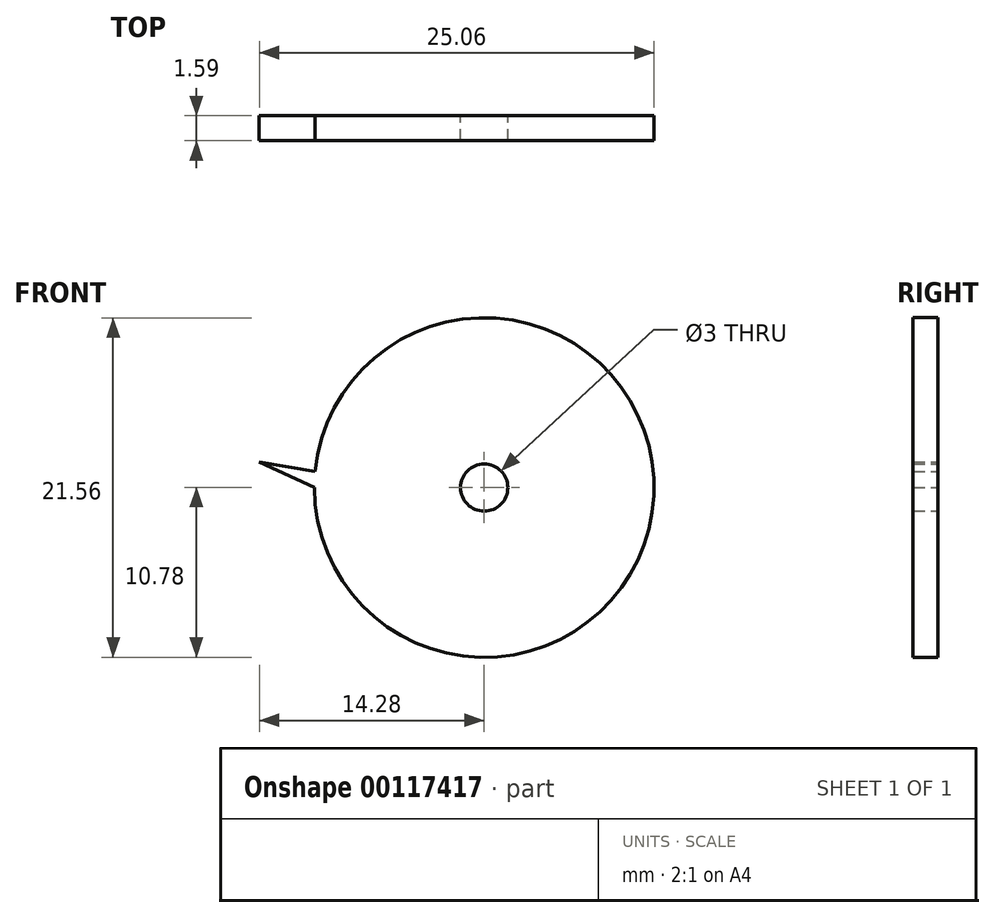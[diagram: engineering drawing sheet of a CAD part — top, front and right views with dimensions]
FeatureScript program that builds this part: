
annotation { "Feature Type Name" : "Feature", "Feature Type Description" : "" }
export const myFeature = defineFeature(function(context is Context, id is Id, definition is map)
    precondition{}
    {
        {
            var Q0;
            Q0=qCreatedBy(makeId("Front.planeOp"),FACE);
            var sketch = newSketch(context, id + "F0", { "sketchPlane" : qUnion([Q0])});
            skCircle(sketch, "E0", {"center": v(0, 0) * mm, "radius": 10.78 * mm});
            skLineSegment(sketch, "E1", {"start": v(-10.78, 0) * mm, "end": v(-14.28, 1.63) * mm});
            skPoint(sketch, "E2.endSnap0", {"position": v(-12.53, 0.82) * mm});
            skLineSegment(sketch, "E3", {"start": v(-14.28, 1.63) * mm, "end": v(-10.74, 1) * mm});
            skCircle(sketch, "E4", {"center": v(0, 0) * mm, "radius": 1.5 * mm});
            skLineSegment(sketch, "E5", {"start": v(-23.85, 0) * mm, "end": v(-3.39, 0) * mm});
            skSolve(sketch);
        }
        {
            var Q0;
            Q0 = qSketchRegion(id + "F0", true);
            extrude(context, id + "F1", {"entities" : qUnion([Q0]), "depth" : 1.59 * mm});
        }
        {
            var Q0;
            Q0 = qSketchRegion(id + "F0", true);
            extrude(context, id + "F2", {"entities" : qUnion([Q0]), "operationType" : NewBodyOperationType.ADD, "depth" : 1 / 406.4 * mm});
        }
    });
